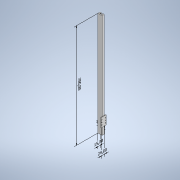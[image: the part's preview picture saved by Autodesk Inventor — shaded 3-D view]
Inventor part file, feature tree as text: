
AUTODESK INVENTOR PART (.ipt)
format: ipt  version: 2021 (Build 250183000, 183)  size: 208,896 bytes
history: native  units: mm
features: other x5, extrude x5, sketch x5, thicken_offset x1
ambient origin geometry x8: Origin, YZ Plane, XZ Plane, XY Plane, X Axis, Y Axis, Z Axis, Center Point
bodies: Solid1 (feature_tree)
feature tree (16):
  other  "Annotations"
  extrude  "Extrusion1"  Depth=5.0mm
  extrude  "Extrusion2"  Depth=5.0mm
  extrude  "Extrusion3"  Depth=15.0mm
  extrude  "Extrusion4"  Depth=5.0mm
  extrude  "Extrusion5"  Depth=5.0mm
  thicken_offset  "Thicken1"
  sketch  "Sketch1"  dims[d0=16.0mm d1=5.0mm]
  sketch  "Sketch2"  dims[d2=4.0mm d3=5.0mm]
  sketch  "Sketch3"  dims[d4=10.0mm d5=15.0mm]
  sketch  "Sketch4"  dims[d6=26.0mm d11=5.0mm]
  sketch  "Sketch5"  dims[d12=4.0mm d13=5.0mm d14=10.0mm d15=15.0mm d16=500.0mm d17=0.0mm d18=80.0mm d19=15.0mm d20=20.0mm d21=30.0mm d22=55.0mm d23=60.0mm d24=10.0mm d25=20.0mm d26=20.0mm d27=35.0mm d28=20.0mm d33=10.0mm d34=10.0mm d35=10.0mm d36=10.0mm d37=3.0mm d38=0.0mm d39=3.0mm d40=0.0mm d41=9.0mm d42=9.0mm d43=3.0mm d44=0.0mm d48=5.0mm d49=5.0mm d50=5.0mm d51=4.5mm d52=5.0mm d53=5.0mm d54=5.0mm d55=3.0mm d56=0.0mm d67=200.0mm d68=200.0mm d57=0.0mm d58=10.0mm d59=15.0mm d60=24.0mm d61=0.0mm d62=10.0mm d63=10.0mm d64=0.0mm d65=10.0mm d66=700.0mm]
  other  "Linear Dimension 1"
  other  "Linear Dimension 2"
  other  "Linear Dimension 3"
  other  "Linear Dimension 4"
